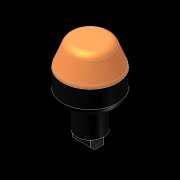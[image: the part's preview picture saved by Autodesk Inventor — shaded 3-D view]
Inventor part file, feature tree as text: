
AUTODESK INVENTOR PART (.ipt)
format: ipt  version: unknown  size: 261,632 bytes
history: native  units: in
note: dims shown in document units (in); Inventor stores cm internally (conversion verified against a paired STEP export)
features: sketch x5, extrude x4, revolve x1, chamfer x1, fillet x1, projected_geometry x1
ambient origin geometry x8: Origin, YZ Plane, XZ Plane, XY Plane, X Axis, Y Axis, Z Axis, Center Point
feature tree (13):
  sketch  "Sketch1"  dims[d0=0.885in d1=1.622in]
  revolve  "Revolution1"  [1 undecoded]
  extrude  "Extrusion3"  Depth=0.44in
  chamfer  "Chamfer1"  Distance=0.756in Angle=45.0deg
  fillet  "Fillet1"  Radius=0.25in
  extrude  "Extrusion2"  Depth=0.5in
  extrude  "Extrusion4"  Depth=0.587in
  extrude  "Extrusion5"  Depth=0.303in
  sketch  "Sketch2"  dims[d2=0.922in d3=0.44in]
  sketch  "Sketch3"  dims[d5=90.0deg d8=0.756in d9=0.295in d10=45.0deg d11=0.25in]
  sketch  "Sketch4"  dims[d12=0.14in d13=0.5in]
  projected_geometry  "Projected Loop1"
  sketch  "Sketch5"  dims[d14=0.086in d15=0.0in d16=0.587in d17=0.303in d18=0.355in d19=0.0in d22=45.0deg d23=0.355in d24=0.14in d25=0.355in d26=0.0in d27=0.1957in d28=0.005in d29=0.005in d30=0.1in d31=0.0in]
note: 1 required parameter value undecoded (feature->parameter linkage not recoverable at this tier; creation-order binding heuristic only, values carry confidence <= 0.55)
